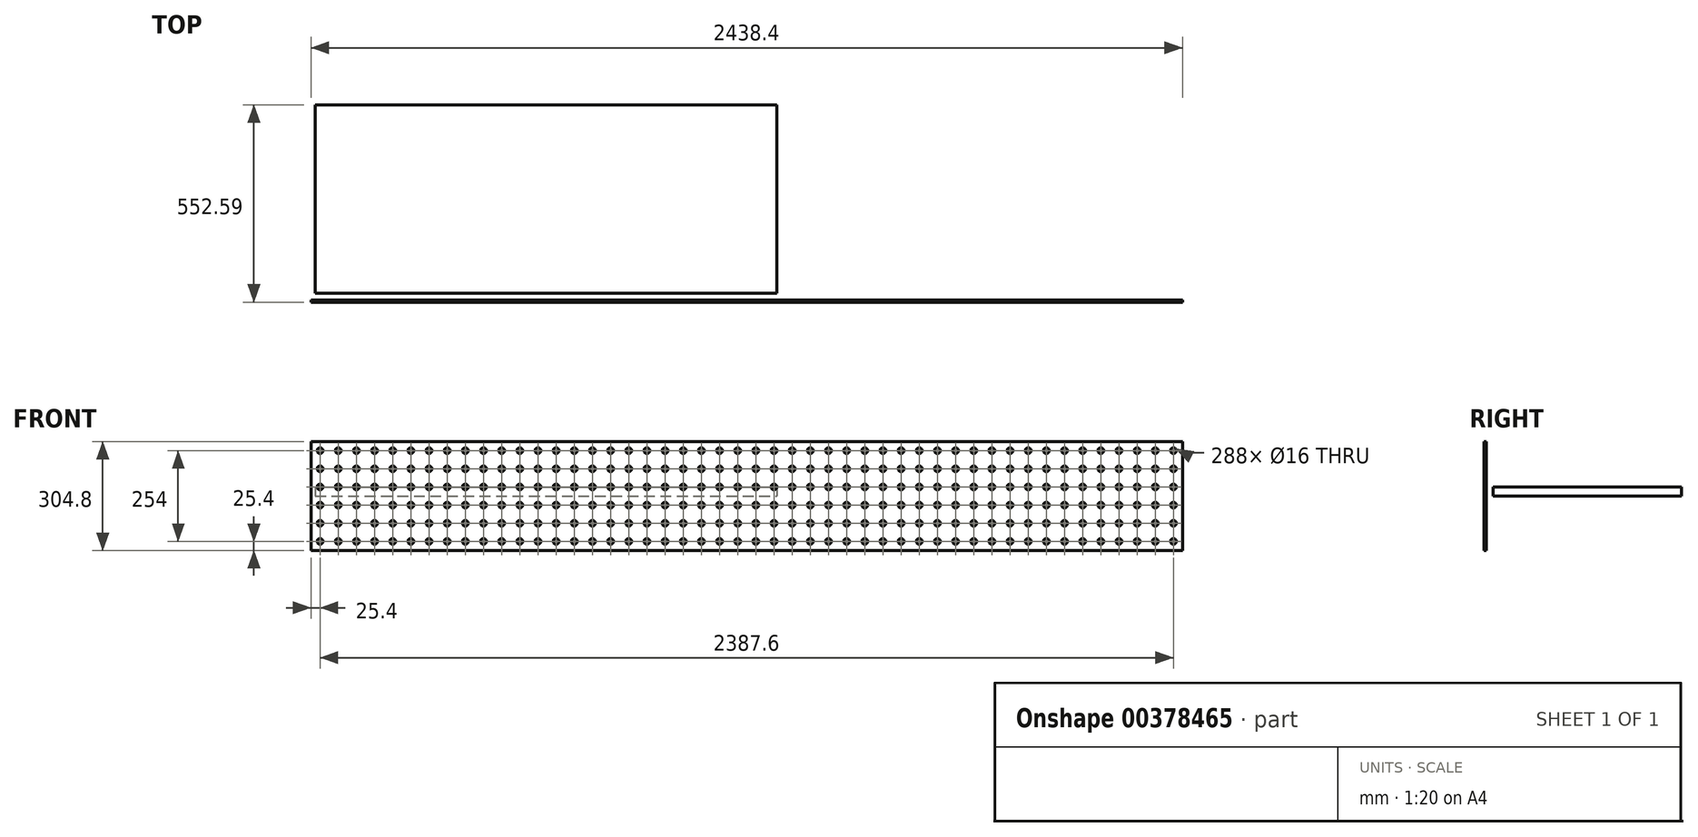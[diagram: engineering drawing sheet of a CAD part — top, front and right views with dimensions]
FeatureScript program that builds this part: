
annotation { "Feature Type Name" : "Feature", "Feature Type Description" : "" }
export const myFeature = defineFeature(function(context is Context, id is Id, definition is map)
    precondition{}
    {
        {
            var Q0;
            Q0=qCreatedBy(makeId("Front.planeOp"),FACE);
            var sketch = newSketch(context, id + "F0", { "sketchPlane" : qUnion([Q0])});
            skLineSegment(sketch, "E0.bottom", {"start": v(1219.2, 152.4) * mm, "end": v(-1219.2, 152.4) * mm});
            skLineSegment(sketch, "E0.top", {"start": v(1219.2, -152.4) * mm, "end": v(-1219.2, -152.4) * mm});
            skLineSegment(sketch, "E0.left", {"start": v(1219.2, 152.4) * mm, "end": v(1219.2, -152.4) * mm});
            skLineSegment(sketch, "E0.right", {"start": v(-1219.2, 152.4) * mm, "end": v(-1219.2, -152.4) * mm});
            skPoint(sketch, "E0.middle", {"position": v(0, 0) * mm});
            skCircle(sketch, "E1", {"center": v(-1193.8, -127) * mm, "radius": 8 * mm});
            skCircle(sketch, "E2.0.1.0", {"center": v(-1193.8, -76.2) * mm, "radius": 8 * mm});
            skCircle(sketch, "E2.0.2.0", {"center": v(-1193.8, -25.4) * mm, "radius": 8 * mm});
            skCircle(sketch, "E2.0.3.0", {"center": v(-1193.8, 25.4) * mm, "radius": 8 * mm});
            skCircle(sketch, "E2.0.4.0", {"center": v(-1193.8, 76.2) * mm, "radius": 8 * mm});
            skCircle(sketch, "E2.0.5.0", {"center": v(-1193.8, 127) * mm, "radius": 8 * mm});
            skCircle(sketch, "E2.1.0.0", {"center": v(-1143, -127) * mm, "radius": 8 * mm});
            skCircle(sketch, "E2.1.1.0", {"center": v(-1143, -76.2) * mm, "radius": 8 * mm});
            skCircle(sketch, "E2.1.2.0", {"center": v(-1143, -25.4) * mm, "radius": 8 * mm});
            skCircle(sketch, "E2.1.3.0", {"center": v(-1143, 25.4) * mm, "radius": 8 * mm});
            skCircle(sketch, "E2.1.4.0", {"center": v(-1143, 76.2) * mm, "radius": 8 * mm});
            skCircle(sketch, "E2.1.5.0", {"center": v(-1143, 127) * mm, "radius": 8 * mm});
            skCircle(sketch, "E2.2.0.0", {"center": v(-1092.2, -127) * mm, "radius": 8 * mm});
            skCircle(sketch, "E2.2.1.0", {"center": v(-1092.2, -76.2) * mm, "radius": 8 * mm});
            skCircle(sketch, "E2.2.2.0", {"center": v(-1092.2, -25.4) * mm, "radius": 8 * mm});
            skCircle(sketch, "E2.2.3.0", {"center": v(-1092.2, 25.4) * mm, "radius": 8 * mm});
            skCircle(sketch, "E2.2.4.0", {"center": v(-1092.2, 76.2) * mm, "radius": 8 * mm});
            skCircle(sketch, "E2.2.5.0", {"center": v(-1092.2, 127) * mm, "radius": 8 * mm});
            skCircle(sketch, "E2.3.0.0", {"center": v(-1041.4, -127) * mm, "radius": 8 * mm});
            skCircle(sketch, "E2.3.1.0", {"center": v(-1041.4, -76.2) * mm, "radius": 8 * mm});
            skCircle(sketch, "E2.3.2.0", {"center": v(-1041.4, -25.4) * mm, "radius": 8 * mm});
            skCircle(sketch, "E2.3.3.0", {"center": v(-1041.4, 25.4) * mm, "radius": 8 * mm});
            skCircle(sketch, "E2.3.4.0", {"center": v(-1041.4, 76.2) * mm, "radius": 8 * mm});
            skCircle(sketch, "E2.3.5.0", {"center": v(-1041.4, 127) * mm, "radius": 8 * mm});
            skCircle(sketch, "E2.4.0.0", {"center": v(-990.6, -127) * mm, "radius": 8 * mm});
            skCircle(sketch, "E2.4.1.0", {"center": v(-990.6, -76.2) * mm, "radius": 8 * mm});
            skCircle(sketch, "E2.4.2.0", {"center": v(-990.6, -25.4) * mm, "radius": 8 * mm});
            skCircle(sketch, "E2.4.3.0", {"center": v(-990.6, 25.4) * mm, "radius": 8 * mm});
            skCircle(sketch, "E2.4.4.0", {"center": v(-990.6, 76.2) * mm, "radius": 8 * mm});
            skCircle(sketch, "E2.4.5.0", {"center": v(-990.6, 127) * mm, "radius": 8 * mm});
            skCircle(sketch, "E2.5.0.0", {"center": v(-939.8, -127) * mm, "radius": 8 * mm});
            skCircle(sketch, "E2.5.1.0", {"center": v(-939.8, -76.2) * mm, "radius": 8 * mm});
            skCircle(sketch, "E2.5.2.0", {"center": v(-939.8, -25.4) * mm, "radius": 8 * mm});
            skCircle(sketch, "E2.5.3.0", {"center": v(-939.8, 25.4) * mm, "radius": 8 * mm});
            skCircle(sketch, "E2.5.4.0", {"center": v(-939.8, 76.2) * mm, "radius": 8 * mm});
            skCircle(sketch, "E2.5.5.0", {"center": v(-939.8, 127) * mm, "radius": 8 * mm});
            skCircle(sketch, "E2.6.0.0", {"center": v(-889, -127) * mm, "radius": 8 * mm});
            skCircle(sketch, "E2.6.1.0", {"center": v(-889, -76.2) * mm, "radius": 8 * mm});
            skCircle(sketch, "E2.6.2.0", {"center": v(-889, -25.4) * mm, "radius": 8 * mm});
            skCircle(sketch, "E2.6.3.0", {"center": v(-889, 25.4) * mm, "radius": 8 * mm});
            skCircle(sketch, "E2.6.4.0", {"center": v(-889, 76.2) * mm, "radius": 8 * mm});
            skCircle(sketch, "E2.6.5.0", {"center": v(-889, 127) * mm, "radius": 8 * mm});
            skCircle(sketch, "E2.7.0.0", {"center": v(-838.2, -127) * mm, "radius": 8 * mm});
            skCircle(sketch, "E2.7.1.0", {"center": v(-838.2, -76.2) * mm, "radius": 8 * mm});
            skCircle(sketch, "E2.7.2.0", {"center": v(-838.2, -25.4) * mm, "radius": 8 * mm});
            skCircle(sketch, "E2.7.3.0", {"center": v(-838.2, 25.4) * mm, "radius": 8 * mm});
            skCircle(sketch, "E2.7.4.0", {"center": v(-838.2, 76.2) * mm, "radius": 8 * mm});
            skCircle(sketch, "E2.7.5.0", {"center": v(-838.2, 127) * mm, "radius": 8 * mm});
            skCircle(sketch, "E2.8.0.0", {"center": v(-787.4, -127) * mm, "radius": 8 * mm});
            skCircle(sketch, "E2.8.1.0", {"center": v(-787.4, -76.2) * mm, "radius": 8 * mm});
            skCircle(sketch, "E2.8.2.0", {"center": v(-787.4, -25.4) * mm, "radius": 8 * mm});
            skCircle(sketch, "E2.8.3.0", {"center": v(-787.4, 25.4) * mm, "radius": 8 * mm});
            skCircle(sketch, "E2.8.4.0", {"center": v(-787.4, 76.2) * mm, "radius": 8 * mm});
            skCircle(sketch, "E2.8.5.0", {"center": v(-787.4, 127) * mm, "radius": 8 * mm});
            skCircle(sketch, "E2.9.0.0", {"center": v(-736.6, -127) * mm, "radius": 8 * mm});
            skCircle(sketch, "E2.9.1.0", {"center": v(-736.6, -76.2) * mm, "radius": 8 * mm});
            skCircle(sketch, "E2.9.2.0", {"center": v(-736.6, -25.4) * mm, "radius": 8 * mm});
            skCircle(sketch, "E2.9.3.0", {"center": v(-736.6, 25.4) * mm, "radius": 8 * mm});
            skCircle(sketch, "E2.9.4.0", {"center": v(-736.6, 76.2) * mm, "radius": 8 * mm});
            skCircle(sketch, "E2.9.5.0", {"center": v(-736.6, 127) * mm, "radius": 8 * mm});
            skCircle(sketch, "E2.10.0.0", {"center": v(-685.8, -127) * mm, "radius": 8 * mm});
            skCircle(sketch, "E2.10.1.0", {"center": v(-685.8, -76.2) * mm, "radius": 8 * mm});
            skCircle(sketch, "E2.10.2.0", {"center": v(-685.8, -25.4) * mm, "radius": 8 * mm});
            skCircle(sketch, "E2.10.3.0", {"center": v(-685.8, 25.4) * mm, "radius": 8 * mm});
            skCircle(sketch, "E2.10.4.0", {"center": v(-685.8, 76.2) * mm, "radius": 8 * mm});
            skCircle(sketch, "E2.10.5.0", {"center": v(-685.8, 127) * mm, "radius": 8 * mm});
            skCircle(sketch, "E2.11.0.0", {"center": v(-635, -127) * mm, "radius": 8 * mm});
            skCircle(sketch, "E2.11.1.0", {"center": v(-635, -76.2) * mm, "radius": 8 * mm});
            skCircle(sketch, "E2.11.2.0", {"center": v(-635, -25.4) * mm, "radius": 8 * mm});
            skCircle(sketch, "E2.11.3.0", {"center": v(-635, 25.4) * mm, "radius": 8 * mm});
            skCircle(sketch, "E2.11.4.0", {"center": v(-635, 76.2) * mm, "radius": 8 * mm});
            skCircle(sketch, "E2.11.5.0", {"center": v(-635, 127) * mm, "radius": 8 * mm});
            skCircle(sketch, "E2.12.0.0", {"center": v(-584.2, -127) * mm, "radius": 8 * mm});
            skCircle(sketch, "E2.12.1.0", {"center": v(-584.2, -76.2) * mm, "radius": 8 * mm});
            skCircle(sketch, "E2.12.2.0", {"center": v(-584.2, -25.4) * mm, "radius": 8 * mm});
            skCircle(sketch, "E2.12.3.0", {"center": v(-584.2, 25.4) * mm, "radius": 8 * mm});
            skCircle(sketch, "E2.12.4.0", {"center": v(-584.2, 76.2) * mm, "radius": 8 * mm});
            skCircle(sketch, "E2.12.5.0", {"center": v(-584.2, 127) * mm, "radius": 8 * mm});
            skCircle(sketch, "E2.13.0.0", {"center": v(-533.4, -127) * mm, "radius": 8 * mm});
            skCircle(sketch, "E2.13.1.0", {"center": v(-533.4, -76.2) * mm, "radius": 8 * mm});
            skCircle(sketch, "E2.13.2.0", {"center": v(-533.4, -25.4) * mm, "radius": 8 * mm});
            skCircle(sketch, "E2.13.3.0", {"center": v(-533.4, 25.4) * mm, "radius": 8 * mm});
            skCircle(sketch, "E2.13.4.0", {"center": v(-533.4, 76.2) * mm, "radius": 8 * mm});
            skCircle(sketch, "E2.13.5.0", {"center": v(-533.4, 127) * mm, "radius": 8 * mm});
            skCircle(sketch, "E2.14.0.0", {"center": v(-482.6, -127) * mm, "radius": 8 * mm});
            skCircle(sketch, "E2.14.1.0", {"center": v(-482.6, -76.2) * mm, "radius": 8 * mm});
            skCircle(sketch, "E2.14.2.0", {"center": v(-482.6, -25.4) * mm, "radius": 8 * mm});
            skCircle(sketch, "E2.14.3.0", {"center": v(-482.6, 25.4) * mm, "radius": 8 * mm});
            skCircle(sketch, "E2.14.4.0", {"center": v(-482.6, 76.2) * mm, "radius": 8 * mm});
            skCircle(sketch, "E2.14.5.0", {"center": v(-482.6, 127) * mm, "radius": 8 * mm});
            skCircle(sketch, "E2.15.0.0", {"center": v(-431.8, -127) * mm, "radius": 8 * mm});
            skCircle(sketch, "E2.15.1.0", {"center": v(-431.8, -76.2) * mm, "radius": 8 * mm});
            skCircle(sketch, "E2.15.2.0", {"center": v(-431.8, -25.4) * mm, "radius": 8 * mm});
            skCircle(sketch, "E2.15.3.0", {"center": v(-431.8, 25.4) * mm, "radius": 8 * mm});
            skCircle(sketch, "E2.15.4.0", {"center": v(-431.8, 76.2) * mm, "radius": 8 * mm});
            skCircle(sketch, "E2.15.5.0", {"center": v(-431.8, 127) * mm, "radius": 8 * mm});
            skCircle(sketch, "E2.16.0.0", {"center": v(-381, -127) * mm, "radius": 8 * mm});
            skCircle(sketch, "E2.16.1.0", {"center": v(-381, -76.2) * mm, "radius": 8 * mm});
            skCircle(sketch, "E2.16.2.0", {"center": v(-381, -25.4) * mm, "radius": 8 * mm});
            skCircle(sketch, "E2.16.3.0", {"center": v(-381, 25.4) * mm, "radius": 8 * mm});
            skCircle(sketch, "E2.16.4.0", {"center": v(-381, 76.2) * mm, "radius": 8 * mm});
            skCircle(sketch, "E2.16.5.0", {"center": v(-381, 127) * mm, "radius": 8 * mm});
            skCircle(sketch, "E2.17.0.0", {"center": v(-330.2, -127) * mm, "radius": 8 * mm});
            skCircle(sketch, "E2.17.1.0", {"center": v(-330.2, -76.2) * mm, "radius": 8 * mm});
            skCircle(sketch, "E2.17.2.0", {"center": v(-330.2, -25.4) * mm, "radius": 8 * mm});
            skCircle(sketch, "E2.17.3.0", {"center": v(-330.2, 25.4) * mm, "radius": 8 * mm});
            skCircle(sketch, "E2.17.4.0", {"center": v(-330.2, 76.2) * mm, "radius": 8 * mm});
            skCircle(sketch, "E2.17.5.0", {"center": v(-330.2, 127) * mm, "radius": 8 * mm});
            skCircle(sketch, "E2.18.0.0", {"center": v(-279.4, -127) * mm, "radius": 8 * mm});
            skCircle(sketch, "E2.18.1.0", {"center": v(-279.4, -76.2) * mm, "radius": 8 * mm});
            skCircle(sketch, "E2.18.2.0", {"center": v(-279.4, -25.4) * mm, "radius": 8 * mm});
            skCircle(sketch, "E2.18.3.0", {"center": v(-279.4, 25.4) * mm, "radius": 8 * mm});
            skCircle(sketch, "E2.18.4.0", {"center": v(-279.4, 76.2) * mm, "radius": 8 * mm});
            skCircle(sketch, "E2.18.5.0", {"center": v(-279.4, 127) * mm, "radius": 8 * mm});
            skCircle(sketch, "E2.19.0.0", {"center": v(-228.6, -127) * mm, "radius": 8 * mm});
            skCircle(sketch, "E2.19.1.0", {"center": v(-228.6, -76.2) * mm, "radius": 8 * mm});
            skCircle(sketch, "E2.19.2.0", {"center": v(-228.6, -25.4) * mm, "radius": 8 * mm});
            skCircle(sketch, "E2.19.3.0", {"center": v(-228.6, 25.4) * mm, "radius": 8 * mm});
            skCircle(sketch, "E2.19.4.0", {"center": v(-228.6, 76.2) * mm, "radius": 8 * mm});
            skCircle(sketch, "E2.19.5.0", {"center": v(-228.6, 127) * mm, "radius": 8 * mm});
            skCircle(sketch, "E2.20.0.0", {"center": v(-177.8, -127) * mm, "radius": 8 * mm});
            skCircle(sketch, "E2.20.1.0", {"center": v(-177.8, -76.2) * mm, "radius": 8 * mm});
            skCircle(sketch, "E2.20.2.0", {"center": v(-177.8, -25.4) * mm, "radius": 8 * mm});
            skCircle(sketch, "E2.20.3.0", {"center": v(-177.8, 25.4) * mm, "radius": 8 * mm});
            skCircle(sketch, "E2.20.4.0", {"center": v(-177.8, 76.2) * mm, "radius": 8 * mm});
            skCircle(sketch, "E2.20.5.0", {"center": v(-177.8, 127) * mm, "radius": 8 * mm});
            skCircle(sketch, "E2.21.0.0", {"center": v(-127, -127) * mm, "radius": 8 * mm});
            skCircle(sketch, "E2.21.1.0", {"center": v(-127, -76.2) * mm, "radius": 8 * mm});
            skCircle(sketch, "E2.21.2.0", {"center": v(-127, -25.4) * mm, "radius": 8 * mm});
            skCircle(sketch, "E2.21.3.0", {"center": v(-127, 25.4) * mm, "radius": 8 * mm});
            skCircle(sketch, "E2.21.4.0", {"center": v(-127, 76.2) * mm, "radius": 8 * mm});
            skCircle(sketch, "E2.21.5.0", {"center": v(-127, 127) * mm, "radius": 8 * mm});
            skCircle(sketch, "E2.22.0.0", {"center": v(-76.2, -127) * mm, "radius": 8 * mm});
            skCircle(sketch, "E2.22.1.0", {"center": v(-76.2, -76.2) * mm, "radius": 8 * mm});
            skCircle(sketch, "E2.22.2.0", {"center": v(-76.2, -25.4) * mm, "radius": 8 * mm});
            skCircle(sketch, "E2.22.3.0", {"center": v(-76.2, 25.4) * mm, "radius": 8 * mm});
            skCircle(sketch, "E2.22.4.0", {"center": v(-76.2, 76.2) * mm, "radius": 8 * mm});
            skCircle(sketch, "E2.22.5.0", {"center": v(-76.2, 127) * mm, "radius": 8 * mm});
            skCircle(sketch, "E2.23.0.0", {"center": v(-25.4, -127) * mm, "radius": 8 * mm});
            skCircle(sketch, "E2.23.1.0", {"center": v(-25.4, -76.2) * mm, "radius": 8 * mm});
            skCircle(sketch, "E2.23.2.0", {"center": v(-25.4, -25.4) * mm, "radius": 8 * mm});
            skCircle(sketch, "E2.23.3.0", {"center": v(-25.4, 25.4) * mm, "radius": 8 * mm});
            skCircle(sketch, "E2.23.4.0", {"center": v(-25.4, 76.2) * mm, "radius": 8 * mm});
            skCircle(sketch, "E2.23.5.0", {"center": v(-25.4, 127) * mm, "radius": 8 * mm});
            skCircle(sketch, "E2.24.0.0", {"center": v(25.4, -127) * mm, "radius": 8 * mm});
            skCircle(sketch, "E2.24.1.0", {"center": v(25.4, -76.2) * mm, "radius": 8 * mm});
            skCircle(sketch, "E2.24.2.0", {"center": v(25.4, -25.4) * mm, "radius": 8 * mm});
            skCircle(sketch, "E2.24.3.0", {"center": v(25.4, 25.4) * mm, "radius": 8 * mm});
            skCircle(sketch, "E2.24.4.0", {"center": v(25.4, 76.2) * mm, "radius": 8 * mm});
            skCircle(sketch, "E2.24.5.0", {"center": v(25.4, 127) * mm, "radius": 8 * mm});
            skCircle(sketch, "E2.25.0.0", {"center": v(76.2, -127) * mm, "radius": 8 * mm});
            skCircle(sketch, "E2.25.1.0", {"center": v(76.2, -76.2) * mm, "radius": 8 * mm});
            skCircle(sketch, "E2.25.2.0", {"center": v(76.2, -25.4) * mm, "radius": 8 * mm});
            skCircle(sketch, "E2.25.3.0", {"center": v(76.2, 25.4) * mm, "radius": 8 * mm});
            skCircle(sketch, "E2.25.4.0", {"center": v(76.2, 76.2) * mm, "radius": 8 * mm});
            skCircle(sketch, "E2.25.5.0", {"center": v(76.2, 127) * mm, "radius": 8 * mm});
            skCircle(sketch, "E2.26.0.0", {"center": v(127, -127) * mm, "radius": 8 * mm});
            skCircle(sketch, "E2.26.1.0", {"center": v(127, -76.2) * mm, "radius": 8 * mm});
            skCircle(sketch, "E2.26.2.0", {"center": v(127, -25.4) * mm, "radius": 8 * mm});
            skCircle(sketch, "E2.26.3.0", {"center": v(127, 25.4) * mm, "radius": 8 * mm});
            skCircle(sketch, "E2.26.4.0", {"center": v(127, 76.2) * mm, "radius": 8 * mm});
            skCircle(sketch, "E2.26.5.0", {"center": v(127, 127) * mm, "radius": 8 * mm});
            skCircle(sketch, "E2.27.0.0", {"center": v(177.8, -127) * mm, "radius": 8 * mm});
            skCircle(sketch, "E2.27.1.0", {"center": v(177.8, -76.2) * mm, "radius": 8 * mm});
            skCircle(sketch, "E2.27.2.0", {"center": v(177.8, -25.4) * mm, "radius": 8 * mm});
            skCircle(sketch, "E2.27.3.0", {"center": v(177.8, 25.4) * mm, "radius": 8 * mm});
            skCircle(sketch, "E2.27.4.0", {"center": v(177.8, 76.2) * mm, "radius": 8 * mm});
            skCircle(sketch, "E2.27.5.0", {"center": v(177.8, 127) * mm, "radius": 8 * mm});
            skCircle(sketch, "E2.28.0.0", {"center": v(228.6, -127) * mm, "radius": 8 * mm});
            skCircle(sketch, "E2.28.1.0", {"center": v(228.6, -76.2) * mm, "radius": 8 * mm});
            skCircle(sketch, "E2.28.2.0", {"center": v(228.6, -25.4) * mm, "radius": 8 * mm});
            skCircle(sketch, "E2.28.3.0", {"center": v(228.6, 25.4) * mm, "radius": 8 * mm});
            skCircle(sketch, "E2.28.4.0", {"center": v(228.6, 76.2) * mm, "radius": 8 * mm});
            skCircle(sketch, "E2.28.5.0", {"center": v(228.6, 127) * mm, "radius": 8 * mm});
            skCircle(sketch, "E2.29.0.0", {"center": v(279.4, -127) * mm, "radius": 8 * mm});
            skCircle(sketch, "E2.29.1.0", {"center": v(279.4, -76.2) * mm, "radius": 8 * mm});
            skCircle(sketch, "E2.29.2.0", {"center": v(279.4, -25.4) * mm, "radius": 8 * mm});
            skCircle(sketch, "E2.29.3.0", {"center": v(279.4, 25.4) * mm, "radius": 8 * mm});
            skCircle(sketch, "E2.29.4.0", {"center": v(279.4, 76.2) * mm, "radius": 8 * mm});
            skCircle(sketch, "E2.29.5.0", {"center": v(279.4, 127) * mm, "radius": 8 * mm});
            skCircle(sketch, "E2.30.0.0", {"center": v(330.2, -127) * mm, "radius": 8 * mm});
            skCircle(sketch, "E2.30.1.0", {"center": v(330.2, -76.2) * mm, "radius": 8 * mm});
            skCircle(sketch, "E2.30.2.0", {"center": v(330.2, -25.4) * mm, "radius": 8 * mm});
            skCircle(sketch, "E2.30.3.0", {"center": v(330.2, 25.4) * mm, "radius": 8 * mm});
            skCircle(sketch, "E2.30.4.0", {"center": v(330.2, 76.2) * mm, "radius": 8 * mm});
            skCircle(sketch, "E2.30.5.0", {"center": v(330.2, 127) * mm, "radius": 8 * mm});
            skCircle(sketch, "E2.31.0.0", {"center": v(381, -127) * mm, "radius": 8 * mm});
            skCircle(sketch, "E2.31.1.0", {"center": v(381, -76.2) * mm, "radius": 8 * mm});
            skCircle(sketch, "E2.31.2.0", {"center": v(381, -25.4) * mm, "radius": 8 * mm});
            skCircle(sketch, "E2.31.3.0", {"center": v(381, 25.4) * mm, "radius": 8 * mm});
            skCircle(sketch, "E2.31.4.0", {"center": v(381, 76.2) * mm, "radius": 8 * mm});
            skCircle(sketch, "E2.31.5.0", {"center": v(381, 127) * mm, "radius": 8 * mm});
            skCircle(sketch, "E2.32.0.0", {"center": v(431.8, -127) * mm, "radius": 8 * mm});
            skCircle(sketch, "E2.32.1.0", {"center": v(431.8, -76.2) * mm, "radius": 8 * mm});
            skCircle(sketch, "E2.32.2.0", {"center": v(431.8, -25.4) * mm, "radius": 8 * mm});
            skCircle(sketch, "E2.32.3.0", {"center": v(431.8, 25.4) * mm, "radius": 8 * mm});
            skCircle(sketch, "E2.32.4.0", {"center": v(431.8, 76.2) * mm, "radius": 8 * mm});
            skCircle(sketch, "E2.32.5.0", {"center": v(431.8, 127) * mm, "radius": 8 * mm});
            skCircle(sketch, "E2.33.0.0", {"center": v(482.6, -127) * mm, "radius": 8 * mm});
            skCircle(sketch, "E2.33.1.0", {"center": v(482.6, -76.2) * mm, "radius": 8 * mm});
            skCircle(sketch, "E2.33.2.0", {"center": v(482.6, -25.4) * mm, "radius": 8 * mm});
            skCircle(sketch, "E2.33.3.0", {"center": v(482.6, 25.4) * mm, "radius": 8 * mm});
            skCircle(sketch, "E2.33.4.0", {"center": v(482.6, 76.2) * mm, "radius": 8 * mm});
            skCircle(sketch, "E2.33.5.0", {"center": v(482.6, 127) * mm, "radius": 8 * mm});
            skCircle(sketch, "E2.34.0.0", {"center": v(533.4, -127) * mm, "radius": 8 * mm});
            skCircle(sketch, "E2.34.1.0", {"center": v(533.4, -76.2) * mm, "radius": 8 * mm});
            skCircle(sketch, "E2.34.2.0", {"center": v(533.4, -25.4) * mm, "radius": 8 * mm});
            skCircle(sketch, "E2.34.3.0", {"center": v(533.4, 25.4) * mm, "radius": 8 * mm});
            skCircle(sketch, "E2.34.4.0", {"center": v(533.4, 76.2) * mm, "radius": 8 * mm});
            skCircle(sketch, "E2.34.5.0", {"center": v(533.4, 127) * mm, "radius": 8 * mm});
            skCircle(sketch, "E2.35.0.0", {"center": v(584.2, -127) * mm, "radius": 8 * mm});
            skCircle(sketch, "E2.35.1.0", {"center": v(584.2, -76.2) * mm, "radius": 8 * mm});
            skCircle(sketch, "E2.35.2.0", {"center": v(584.2, -25.4) * mm, "radius": 8 * mm});
            skCircle(sketch, "E2.35.3.0", {"center": v(584.2, 25.4) * mm, "radius": 8 * mm});
            skCircle(sketch, "E2.35.4.0", {"center": v(584.2, 76.2) * mm, "radius": 8 * mm});
            skCircle(sketch, "E2.35.5.0", {"center": v(584.2, 127) * mm, "radius": 8 * mm});
            skCircle(sketch, "E2.36.0.0", {"center": v(635, -127) * mm, "radius": 8 * mm});
            skCircle(sketch, "E2.36.1.0", {"center": v(635, -76.2) * mm, "radius": 8 * mm});
            skCircle(sketch, "E2.36.2.0", {"center": v(635, -25.4) * mm, "radius": 8 * mm});
            skCircle(sketch, "E2.36.3.0", {"center": v(635, 25.4) * mm, "radius": 8 * mm});
            skCircle(sketch, "E2.36.4.0", {"center": v(635, 76.2) * mm, "radius": 8 * mm});
            skCircle(sketch, "E2.36.5.0", {"center": v(635, 127) * mm, "radius": 8 * mm});
            skCircle(sketch, "E2.37.0.0", {"center": v(685.8, -127) * mm, "radius": 8 * mm});
            skCircle(sketch, "E2.37.1.0", {"center": v(685.8, -76.2) * mm, "radius": 8 * mm});
            skCircle(sketch, "E2.37.2.0", {"center": v(685.8, -25.4) * mm, "radius": 8 * mm});
            skCircle(sketch, "E2.37.3.0", {"center": v(685.8, 25.4) * mm, "radius": 8 * mm});
            skCircle(sketch, "E2.37.4.0", {"center": v(685.8, 76.2) * mm, "radius": 8 * mm});
            skCircle(sketch, "E2.37.5.0", {"center": v(685.8, 127) * mm, "radius": 8 * mm});
            skCircle(sketch, "E2.38.0.0", {"center": v(736.6, -127) * mm, "radius": 8 * mm});
            skCircle(sketch, "E2.38.1.0", {"center": v(736.6, -76.2) * mm, "radius": 8 * mm});
            skCircle(sketch, "E2.38.2.0", {"center": v(736.6, -25.4) * mm, "radius": 8 * mm});
            skCircle(sketch, "E2.38.3.0", {"center": v(736.6, 25.4) * mm, "radius": 8 * mm});
            skCircle(sketch, "E2.38.4.0", {"center": v(736.6, 76.2) * mm, "radius": 8 * mm});
            skCircle(sketch, "E2.38.5.0", {"center": v(736.6, 127) * mm, "radius": 8 * mm});
            skCircle(sketch, "E2.39.0.0", {"center": v(787.4, -127) * mm, "radius": 8 * mm});
            skCircle(sketch, "E2.39.1.0", {"center": v(787.4, -76.2) * mm, "radius": 8 * mm});
            skCircle(sketch, "E2.39.2.0", {"center": v(787.4, -25.4) * mm, "radius": 8 * mm});
            skCircle(sketch, "E2.39.3.0", {"center": v(787.4, 25.4) * mm, "radius": 8 * mm});
            skCircle(sketch, "E2.39.4.0", {"center": v(787.4, 76.2) * mm, "radius": 8 * mm});
            skCircle(sketch, "E2.39.5.0", {"center": v(787.4, 127) * mm, "radius": 8 * mm});
            skCircle(sketch, "E2.40.0.0", {"center": v(838.2, -127) * mm, "radius": 8 * mm});
            skCircle(sketch, "E2.40.1.0", {"center": v(838.2, -76.2) * mm, "radius": 8 * mm});
            skCircle(sketch, "E2.40.2.0", {"center": v(838.2, -25.4) * mm, "radius": 8 * mm});
            skCircle(sketch, "E2.40.3.0", {"center": v(838.2, 25.4) * mm, "radius": 8 * mm});
            skCircle(sketch, "E2.40.4.0", {"center": v(838.2, 76.2) * mm, "radius": 8 * mm});
            skCircle(sketch, "E2.40.5.0", {"center": v(838.2, 127) * mm, "radius": 8 * mm});
            skCircle(sketch, "E2.41.0.0", {"center": v(889, -127) * mm, "radius": 8 * mm});
            skCircle(sketch, "E2.41.1.0", {"center": v(889, -76.2) * mm, "radius": 8 * mm});
            skCircle(sketch, "E2.41.2.0", {"center": v(889, -25.4) * mm, "radius": 8 * mm});
            skCircle(sketch, "E2.41.3.0", {"center": v(889, 25.4) * mm, "radius": 8 * mm});
            skCircle(sketch, "E2.41.4.0", {"center": v(889, 76.2) * mm, "radius": 8 * mm});
            skCircle(sketch, "E2.41.5.0", {"center": v(889, 127) * mm, "radius": 8 * mm});
            skCircle(sketch, "E2.42.0.0", {"center": v(939.8, -127) * mm, "radius": 8 * mm});
            skCircle(sketch, "E2.42.1.0", {"center": v(939.8, -76.2) * mm, "radius": 8 * mm});
            skCircle(sketch, "E2.42.2.0", {"center": v(939.8, -25.4) * mm, "radius": 8 * mm});
            skCircle(sketch, "E2.42.3.0", {"center": v(939.8, 25.4) * mm, "radius": 8 * mm});
            skCircle(sketch, "E2.42.4.0", {"center": v(939.8, 76.2) * mm, "radius": 8 * mm});
            skCircle(sketch, "E2.42.5.0", {"center": v(939.8, 127) * mm, "radius": 8 * mm});
            skCircle(sketch, "E2.43.0.0", {"center": v(990.6, -127) * mm, "radius": 8 * mm});
            skCircle(sketch, "E2.43.1.0", {"center": v(990.6, -76.2) * mm, "radius": 8 * mm});
            skCircle(sketch, "E2.43.2.0", {"center": v(990.6, -25.4) * mm, "radius": 8 * mm});
            skCircle(sketch, "E2.43.3.0", {"center": v(990.6, 25.4) * mm, "radius": 8 * mm});
            skCircle(sketch, "E2.43.4.0", {"center": v(990.6, 76.2) * mm, "radius": 8 * mm});
            skCircle(sketch, "E2.43.5.0", {"center": v(990.6, 127) * mm, "radius": 8 * mm});
            skCircle(sketch, "E2.44.0.0", {"center": v(1041.4, -127) * mm, "radius": 8 * mm});
            skCircle(sketch, "E2.44.1.0", {"center": v(1041.4, -76.2) * mm, "radius": 8 * mm});
            skCircle(sketch, "E2.44.2.0", {"center": v(1041.4, -25.4) * mm, "radius": 8 * mm});
            skCircle(sketch, "E2.44.3.0", {"center": v(1041.4, 25.4) * mm, "radius": 8 * mm});
            skCircle(sketch, "E2.44.4.0", {"center": v(1041.4, 76.2) * mm, "radius": 8 * mm});
            skCircle(sketch, "E2.44.5.0", {"center": v(1041.4, 127) * mm, "radius": 8 * mm});
            skCircle(sketch, "E2.45.0.0", {"center": v(1092.2, -127) * mm, "radius": 8 * mm});
            skCircle(sketch, "E2.45.1.0", {"center": v(1092.2, -76.2) * mm, "radius": 8 * mm});
            skCircle(sketch, "E2.45.2.0", {"center": v(1092.2, -25.4) * mm, "radius": 8 * mm});
            skCircle(sketch, "E2.45.3.0", {"center": v(1092.2, 25.4) * mm, "radius": 8 * mm});
            skCircle(sketch, "E2.45.4.0", {"center": v(1092.2, 76.2) * mm, "radius": 8 * mm});
            skCircle(sketch, "E2.45.5.0", {"center": v(1092.2, 127) * mm, "radius": 8 * mm});
            skCircle(sketch, "E2.46.0.0", {"center": v(1143, -127) * mm, "radius": 8 * mm});
            skCircle(sketch, "E2.46.1.0", {"center": v(1143, -76.2) * mm, "radius": 8 * mm});
            skCircle(sketch, "E2.46.2.0", {"center": v(1143, -25.4) * mm, "radius": 8 * mm});
            skCircle(sketch, "E2.46.3.0", {"center": v(1143, 25.4) * mm, "radius": 8 * mm});
            skCircle(sketch, "E2.46.4.0", {"center": v(1143, 76.2) * mm, "radius": 8 * mm});
            skCircle(sketch, "E2.46.5.0", {"center": v(1143, 127) * mm, "radius": 8 * mm});
            skLineSegment(sketch, "E2.direction1", {"start": v(-1193.8, -127) * mm, "end": v(-1143, -127) * mm, "construction": true});
            skLineSegment(sketch, "E2.direction2", {"start": v(-1193.8, -127) * mm, "end": v(-1193.8, -76.2) * mm, "construction": true});
            skCircle(sketch, "E3.0.47.0", {"center": v(1193.8, -127) * mm, "radius": 8 * mm});
            skCircle(sketch, "E3.0.47.1", {"center": v(1193.8, -76.2) * mm, "radius": 8 * mm});
            skCircle(sketch, "E3.0.47.2", {"center": v(1193.8, -25.4) * mm, "radius": 8 * mm});
            skCircle(sketch, "E3.0.47.3", {"center": v(1193.8, 25.4) * mm, "radius": 8 * mm});
            skCircle(sketch, "E3.0.47.4", {"center": v(1193.8, 76.2) * mm, "radius": 8 * mm});
            skCircle(sketch, "E3.0.47.5", {"center": v(1193.8, 127) * mm, "radius": 8 * mm});
            skSolve(sketch);
        }
        {
            var Q0;
            Q0=makeQuery(id+"F0.imprint","IMPRINT",FACE,{"disambiguationData":[TD([[makeQuery(id+"F0.imprint","IMPRINT",EDGE,{"derivedFrom":sQuery(id+"F0.wireOp",EDGE,"E0.bottom")}),1.0]])]});
            extrude(context, id + "F1", {"entities" : qUnion([Q0]), "endBound" : BoundingType.SYMMETRIC, "depth" : 6.35 * mm});
        }
        {
            var Q0;
            Q0=qCreatedBy(makeId("Top.planeOp"),FACE);
            var sketch = newSketch(context, id + "F2", { "sketchPlane" : qUnion([Q0])});
            skLineSegment(sketch, "E4.bottom", {"start": v(-1207.09, 21.65) * mm, "end": v(83.9, 21.65) * mm});
            skLineSegment(sketch, "E4.top", {"start": v(-1207.09, 549.41) * mm, "end": v(83.9, 549.41) * mm});
            skLineSegment(sketch, "E4.left", {"start": v(-1207.09, 21.65) * mm, "end": v(-1207.09, 549.41) * mm});
            skLineSegment(sketch, "E4.right", {"start": v(83.9, 21.65) * mm, "end": v(83.9, 549.41) * mm});
            skSolve(sketch);
        }
        {
            var Q0;
            Q0 = qSketchRegion(id + "F2", true);
            extrude(context, id + "F3", {"entities" : qUnion([Q0]), "depth" : 25.4 * mm});
        }
    });
